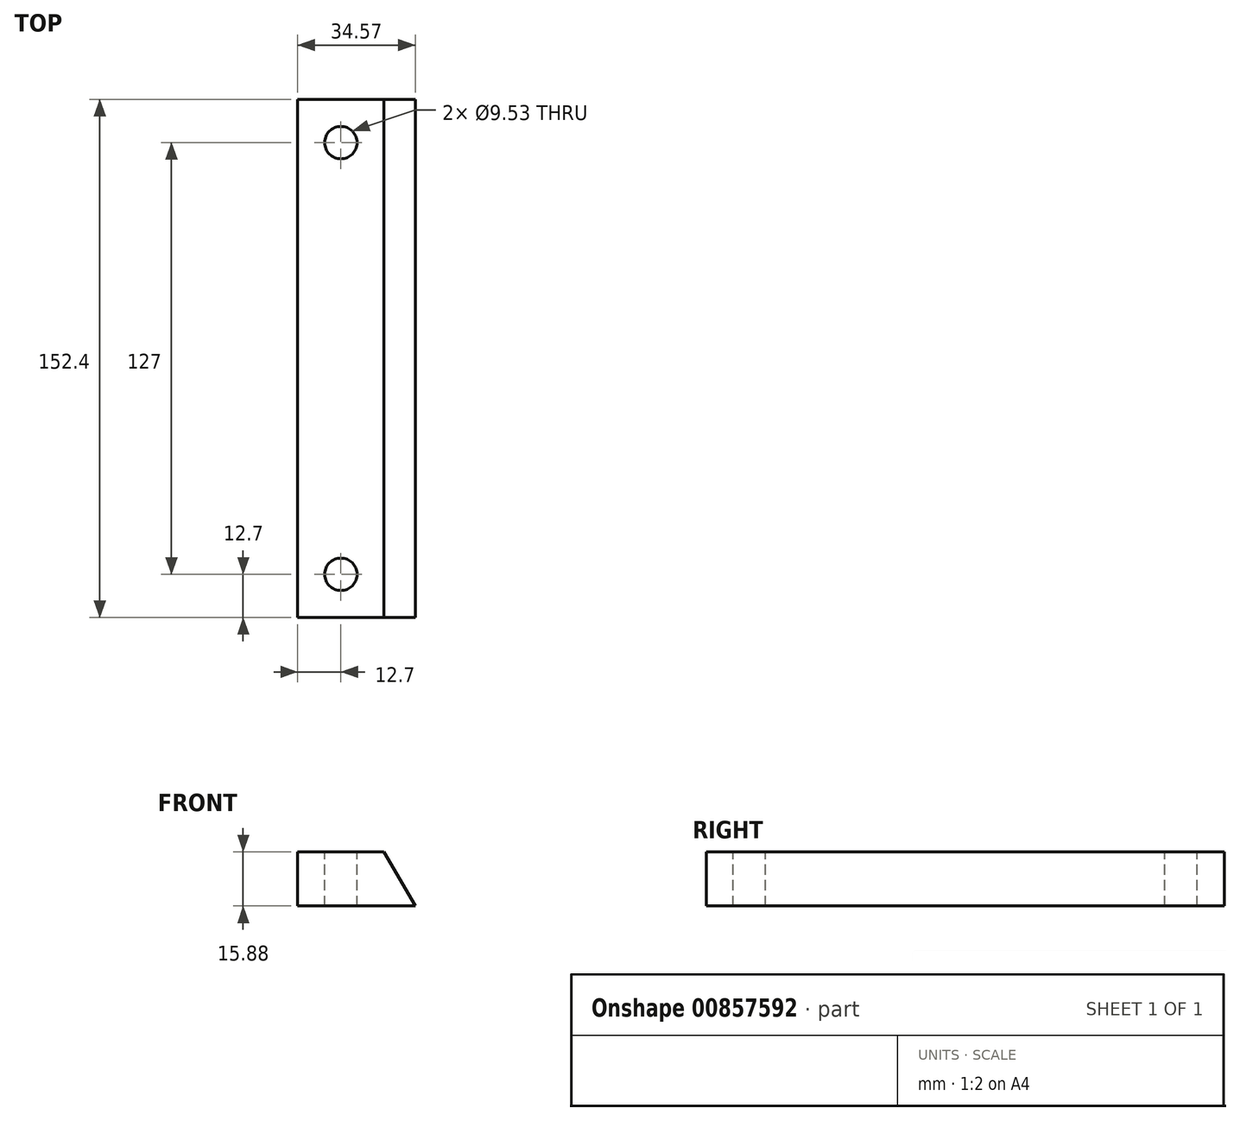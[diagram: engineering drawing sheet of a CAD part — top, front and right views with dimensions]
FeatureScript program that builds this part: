
annotation { "Feature Type Name" : "Feature", "Feature Type Description" : "" }
export const myFeature = defineFeature(function(context is Context, id is Id, definition is map)
    precondition{}
    {
        {
            var Q0;
            Q0=qCreatedBy(makeId("Front.planeOp"),FACE);
            var sketch = newSketch(context, id + "F0", { "sketchPlane" : qUnion([Q0])});
            skLineSegment(sketch, "E0", {"start": v(0, 0) * mm, "end": v(25.4, 0) * mm});
            skLineSegment(sketch, "E1", {"start": v(25.4, 0) * mm, "end": v(34.57, -15.87) * mm});
            skLineSegment(sketch, "E2", {"start": v(34.57, -15.87) * mm, "end": v(0, -15.88) * mm});
            skLineSegment(sketch, "E3", {"start": v(0, -15.88) * mm, "end": v(0, 0) * mm});
            skSolve(sketch);
        }
        {
            var Q0;
            Q0=makeQuery(id+"F0.imprint","IMPRINT",FACE,{"disambiguationData":[TD([[makeQuery(id+"F0.imprint","IMPRINT",EDGE,{"derivedFrom":sQuery(id+"F0.wireOp",EDGE,"E0")}),-1.0]])]});
            extrude(context, id + "F1", {"entities" : qUnion([Q0]), "depth" : 152.4 * mm, "offsetDistance" : 25.4 * mm});
        }
        {
            var Q0;
            Q0=makeQuery(id+"F1.opExtrude","SWEPT_FACE",FACE,{"disambiguationData":[OSD([sQuery(id+"F0.wireOp",EDGE,"E0")])]});
            var sketch = newSketch(context, id + "F2", { "sketchPlane" : qUnion([Q0])});
            skPoint(sketch, "E4", {"position": v(12.7, -139.7) * mm});
            skPoint(sketch, "E4.positionSnap0", {"position": v(12.7, -152.4) * mm});
            skPoint(sketch, "E5", {"position": v(12.7, -12.7) * mm});
            skCircle(sketch, "E6", {"center": v(12.7, -12.7) * mm, "radius": 4.76 * mm});
            skCircle(sketch, "E7", {"center": v(12.7, -139.7) * mm, "radius": 4.76 * mm});
            skSolve(sketch);
        }
        {
            var Q0;
            Q0=makeQuery(id+"F2.imprint","IMPRINT",FACE,{"disambiguationData":[TD([[makeQuery(id+"F2.imprint","IMPRINT",EDGE,{"derivedFrom":sQuery(id+"F2.wireOp",EDGE,"E6")}),1.0]])]});
            var Q1;
            Q1=makeQuery(id+"F2.imprint","IMPRINT",FACE,{"disambiguationData":[TD([[makeQuery(id+"F2.imprint","IMPRINT",EDGE,{"derivedFrom":sQuery(id+"F2.wireOp",EDGE,"E7")}),1.0]])]});
            extrude(context, id + "F3", {"entities" : qUnion([Q0, Q1]), "operationType" : NewBodyOperationType.REMOVE, "oppositeDirection" : true, "depth" : 25.4 * mm, "offsetDistance" : 25.4 * mm});
        }
    });
